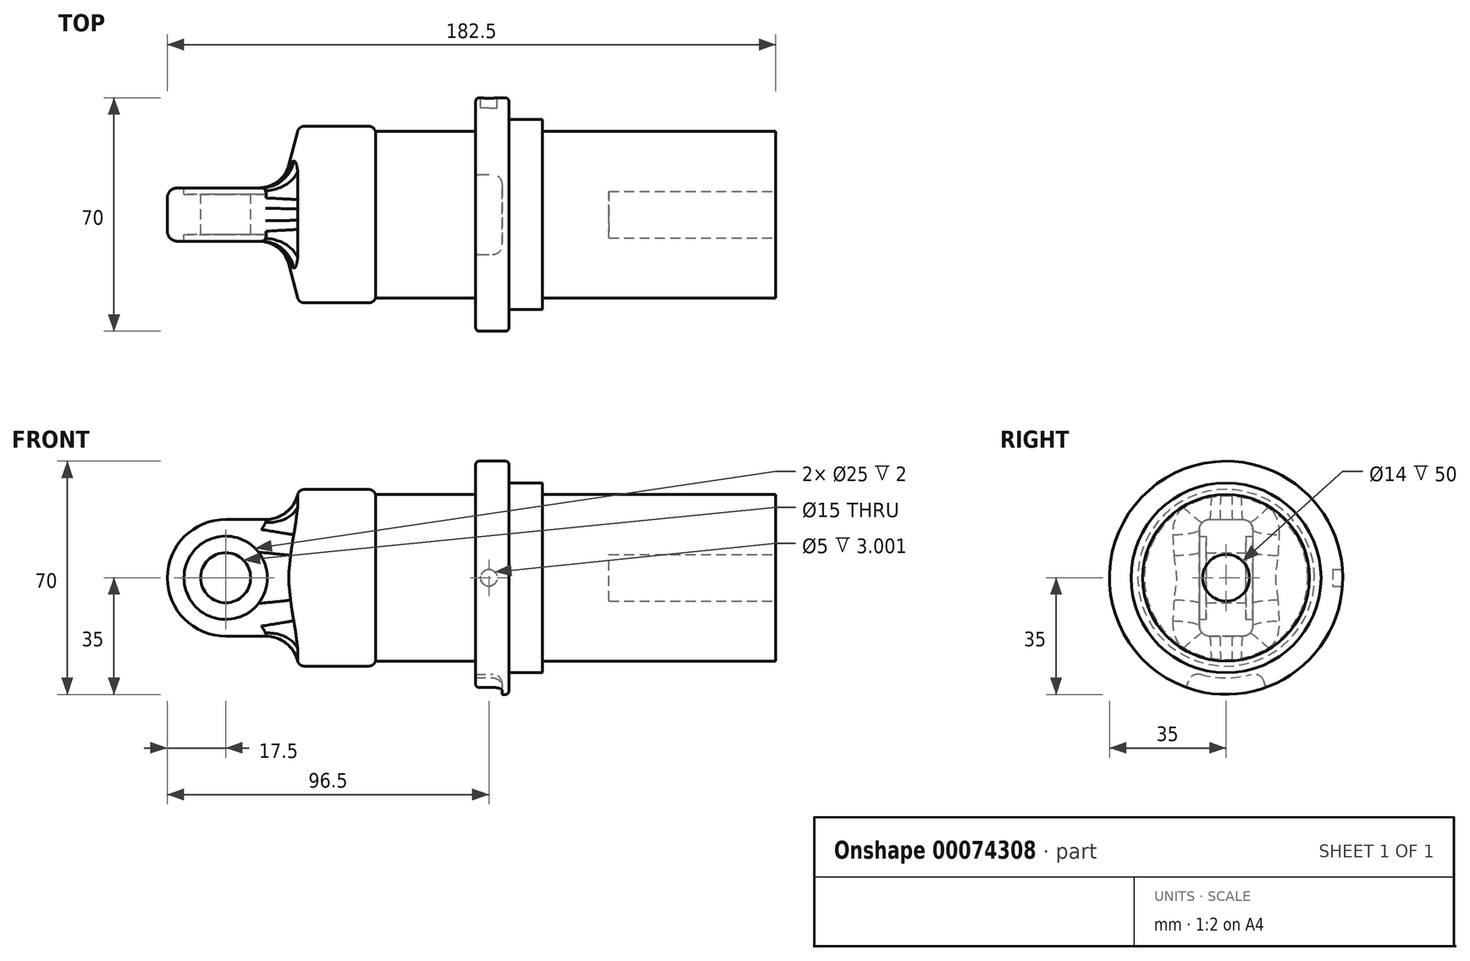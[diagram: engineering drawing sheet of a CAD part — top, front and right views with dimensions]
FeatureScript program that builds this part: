
annotation { "Feature Type Name" : "Feature", "Feature Type Description" : "" }
export const myFeature = defineFeature(function(context is Context, id is Id, definition is map)
    precondition{}
    {
        {
            var Q0;
            Q0=qCreatedBy(makeId("Front.planeOp"),FACE);
            var sketch = newSketch(context, id + "F0", { "sketchPlane" : qUnion([Q0])});
            skArc(sketch, "E0", {"start": v(0, 17.5) * mm, "mid": v(-17.5, 0) * mm, "end": v(0, -17.5) * mm});
            skCircle(sketch, "E1", {"center": v(0, 0) * mm, "radius": 12.5 * mm});
            skLineSegment(sketch, "E2", {"start": v(0, 17.5) * mm, "end": v(25, 17.5) * mm});
            skLineSegment(sketch, "E3", {"start": v(0, -17.5) * mm, "end": v(25, -17.5) * mm});
            skLineSegment(sketch, "E4", {"start": v(25, 17.5) * mm, "end": v(25, -17.5) * mm});
            skSolve(sketch);
        }
        {
            var Q0;
            Q0=makeQuery(id+"F0.imprint","IMPRINT",FACE,{"disambiguationData":[TD([[makeQuery(id+"F0.imprint","IMPRINT",EDGE,{"derivedFrom":sQuery(id+"F0.wireOp",EDGE,"E0")}),1.0]])]});
            extrude(context, id + "F1", {"entities" : qUnion([Q0]), "depth" : 16 * mm, "symmetric" : true});
        }
        {
            var Q0;
            Q0=qCreatedBy(makeId("Top.planeOp"),FACE);
            var sketch = newSketch(context, id + "F2", { "sketchPlane" : qUnion([Q0])});
            skLineSegment(sketch, "E5", {"start": v(0, 0) * mm, "end": v(85.18, 0) * mm, "construction": true});
            skLineSegment(sketch, "E6", {"start": v(45, 0) * mm, "end": v(45, 24.5) * mm});
            skLineSegment(sketch, "E7", {"start": v(43, 26.5) * mm, "end": v(23.54, 26.5) * mm});
            skLineSegment(sketch, "E8", {"start": v(21.6, 25.01) * mm, "end": v(15, 0) * mm});
            skPoint(sketch, "E9.visualSharp", {"position": v(45, 26.5) * mm});
            skArc(sketch, "E9.filletArc", {"start": v(45, 24.5) * mm, "mid": v(44.41, 25.91) * mm, "end": v(43, 26.5) * mm});
            skPoint(sketch, "E10.visualSharp", {"position": v(22, 26.5) * mm});
            skArc(sketch, "E10.filletArc", {"start": v(23.54, 26.5) * mm, "mid": v(22.32, 26.08) * mm, "end": v(21.6, 25.01) * mm});
            skLineSegment(sketch, "E11", {"start": v(45, 0) * mm, "end": v(15, 0) * mm});
            skSolve(sketch);
        }
        {
            var Q0;
            Q0=makeQuery(id+"F2.imprint","IMPRINT",FACE,{"disambiguationData":[TD([[makeQuery(id+"F2.imprint","IMPRINT",EDGE,{"derivedFrom":sQuery(id+"F2.wireOp",EDGE,"E6")}),1.0]])]});
            var Q1;
            Q1=sQuery(id+"F2.wireOp",EDGE,"E5");
            revolve(context, id + "F3", {"operationType" : NewBodyOperationType.ADD, "entities" : qUnion([Q0]), "axis" : qUnion([Q1]), "revolveType" : RevolveType.FULL});
        }
        {
            var Q0;
            Q0=makeQuery(id+"F1.opExtrude","CAP_EDGE",EDGE,{"disambiguationData":[OSD([sQuery(id+"F0.wireOp",EDGE,"E3")])],"isStart":true});
            var Q1;
            Q1=makeQuery(id+"F1.opExtrude","CAP_EDGE",EDGE,{"disambiguationData":[OSD([sQuery(id+"F0.wireOp",EDGE,"E3")])],"isStart":false});
            fillet(context, id + "F4", {"entities" : qUnion([Q0, Q1]), "radius" : 3 * mm, "tangentPropagation" : true, "allowEdgeOverflow" : false});
        }
        {
            var Q0;
            Q0=makeQuery(id+"F3.boolean.opBoolean","INTERSECT",EDGE,{"derivedFrom":[makeQuery(id+"F1.opExtrude","SWEPT_FACE",FACE,{"disambiguationData":[OSD([sQuery(id+"F0.wireOp",EDGE,"E3")])]}),makeQuery(id+"F3.opRevolve","SWEPT_FACE",FACE,{"disambiguationData":[OSD([sQuery(id+"F2.wireOp",EDGE,"E8")])]})]});
            fillet(context, id + "F5", {"entities" : qUnion([Q0]), "radius" : 10 * mm, "tangentPropagation" : true, "allowEdgeOverflow" : false});
        }
        {
            var Q0;
            Q0=qCreatedBy(makeId("Front.planeOp"),FACE);
            var sketch = newSketch(context, id + "F6", { "sketchPlane" : qUnion([Q0])});
            skCircle(sketch, "E12", {"center": v(0, 0) * mm, "radius": 7.5 * mm});
            skCircle(sketch, "E13", {"center": v(0, 0) * mm, "radius": 12.5 * mm});
            skSolve(sketch);
        }
        {
            var Q0;
            Q0 = qSketchRegion(id + "F6", true);
            extrude(context, id + "F7", {"entities" : qUnion([Q0]), "operationType" : NewBodyOperationType.ADD, "depth" : 12 * mm, "symmetric" : true});
        }
        {
            var Q0;
            Q0=makeQuery(id+"F3.opRevolve","SWEPT_FACE",FACE,{"disambiguationData":[OSD([sQuery(id+"F2.wireOp",EDGE,"E6")])]});
            var sketch = newSketch(context, id + "F8", { "sketchPlane" : qUnion([Q0])});
            skCircle(sketch, "E14", {"center": v(0, 0) * mm, "radius": 25 * mm});
            skSolve(sketch);
        }
        {
            var Q0;
            Q0 = qSketchRegion(id + "F8", true);
            extrude(context, id + "F9", {"entities" : qUnion([Q0]), "operationType" : NewBodyOperationType.ADD, "depth" : 120 * mm});
        }
        {
            var Q0;
            Q0=makeQuery(id+"F9.opExtrude","CAP_FACE",FACE,{"disambiguationData":[OSD([sQuery(id+"F8.wireOp",EDGE,"E14")])],"isStart":false});
            var sketch = newSketch(context, id + "F10", { "sketchPlane" : qUnion([Q0])});
            skCircle(sketch, "E15", {"center": v(0, 0) * mm, "radius": 7 * mm});
            skSolve(sketch);
        }
        {
            var Q0;
            Q0 = qSketchRegion(id + "F10", true);
            extrude(context, id + "F11", {"entities" : qUnion([Q0]), "operationType" : NewBodyOperationType.REMOVE, "oppositeDirection" : true, "depth" : 50 * mm});
        }
        {
            var Q0;
            Q0=makeQuery(id+"F9.opExtrude","CAP_FACE",FACE,{"disambiguationData":[OSD([sQuery(id+"F8.wireOp",EDGE,"E14")])],"isStart":false});
            cPlane(context, id + "F12", {"entities" : qUnion([Q0]), "cplaneType" : CPlaneType.OFFSET, "offset" : 80 * mm, "oppositeDirection" : true, "width" : 150 * mm, "height" : 150 * mm});
        }
        {
            var Q0;
            Q0=qCreatedBy(id+"F12.planeOp",FACE);
            var sketch = newSketch(context, id + "F13", { "sketchPlane" : qUnion([Q0])});
            skCircle(sketch, "E16.0", {"center": v(0, 0) * mm, "radius": 25 * mm});
            skCircle(sketch, "E17", {"center": v(0, 0) * mm, "radius": 28.5 * mm});
            skSolve(sketch);
        }
        {
            var Q0;
            Q0 = qSketchRegion(id + "F13", true);
            extrude(context, id + "F14", {"entities" : qUnion([Q0]), "operationType" : NewBodyOperationType.ADD, "depth" : 10 * mm});
        }
        {
            var Q0;
            Q0=makeQuery(id+"F14.opExtrude","CAP_FACE",FACE,{"disambiguationData":[OSD([sQuery(id+"F13.wireOp",EDGE,"E16.0"),sQuery(id+"F13.wireOp",EDGE,"E17")])],"isStart":true});
            var sketch = newSketch(context, id + "F15", { "sketchPlane" : qUnion([Q0])});
            skCircle(sketch, "E18.0", {"center": v(0, 0) * mm, "radius": 25 * mm});
            skCircle(sketch, "E19", {"center": v(0, 0) * mm, "radius": 35 * mm});
            skSolve(sketch);
        }
        {
            var Q0;
            Q0 = qSketchRegion(id + "F15", true);
            extrude(context, id + "F16", {"entities" : qUnion([Q0]), "operationType" : NewBodyOperationType.ADD, "depth" : 10 * mm});
        }
        {
            var Q0;
            Q0=qCreatedBy(makeId("Front.planeOp"),FACE);
            var sketch = newSketch(context, id + "F17", { "sketchPlane" : qUnion([Q0])});
            skLineSegment(sketch, "E20", {"start": v(0, 0) * mm, "end": v(172.26, 0) * mm, "construction": true});
            skLineSegment(sketch, "E21.0", {"start": v(75, -35) * mm, "end": v(75, 35) * mm, "construction": true});
            skLineSegment(sketch, "E22.bottom", {"start": v(75, -35) * mm, "end": v(83, -35) * mm});
            skLineSegment(sketch, "E22.top", {"start": v(75, -30) * mm, "end": v(83, -30) * mm});
            skLineSegment(sketch, "E22.left", {"start": v(75, -35) * mm, "end": v(75, -30) * mm});
            skLineSegment(sketch, "E22.right", {"start": v(83, -35) * mm, "end": v(83, -30) * mm});
            skSolve(sketch);
        }
        {
            var Q0;
            Q0 = qSketchRegion(id + "F17", true);
            var Q1;
            Q1=sQuery(id+"F17.wireOp",EDGE,"E20");
            revolve(context, id + "F18", {"operationType" : NewBodyOperationType.REMOVE, "entities" : qUnion([Q0]), "axis" : qUnion([Q1]), "revolveType" : RevolveType.SYMMETRIC, "oppositeDirection" : true, "angle" : 40 * degree});
        }
        {
            var Q0;
            Q0=makeQuery(id+"F18.boolean.opBoolean","COPY",EDGE,{"derivedFrom":makeQuery(id+"F18.opRevolve","SWEPT_EDGE",EDGE,{"disambiguationData":[OSD([sQuery(id+"F17.wireOp",EDGE,"E22.top"),sQuery(id+"F17.wireOp",EDGE,"E22.right")])]})});
            var Q1;
            Q1=makeQuery(id+"F18.boolean.opBoolean","COPY",EDGE,{"derivedFrom":makeQuery(id+"F18.opRevolve","CAP_EDGE",EDGE,{"disambiguationData":[OSD([sQuery(id+"F17.wireOp",EDGE,"E22.right")])],"isStart":false})});
            var Q2;
            Q2=makeQuery(id+"F18.boolean.opBoolean","COPY",EDGE,{"derivedFrom":makeQuery(id+"F18.opRevolve","CAP_EDGE",EDGE,{"disambiguationData":[OSD([sQuery(id+"F17.wireOp",EDGE,"E22.top")])],"isStart":false})});
            var Q3;
            Q3=makeQuery(id+"F18.boolean.opBoolean","COPY",EDGE,{"derivedFrom":makeQuery(id+"F18.opRevolve","CAP_EDGE",EDGE,{"disambiguationData":[OSD([sQuery(id+"F17.wireOp",EDGE,"E22.top")])],"isStart":true})});
            var Q4;
            Q4=makeQuery(id+"F18.boolean.opBoolean","COPY",EDGE,{"derivedFrom":makeQuery(id+"F18.opRevolve","CAP_EDGE",EDGE,{"disambiguationData":[OSD([sQuery(id+"F17.wireOp",EDGE,"E22.right")])],"isStart":true})});
            fillet(context, id + "F19", {"entities" : qUnion([Q0, Q1, Q2, Q3, Q4]), "radius" : 3 * mm, "tangentPropagation" : true, "allowEdgeOverflow" : false});
        }
        {
            var Q0;
            Q0=qCreatedBy(makeId("Front.planeOp"),FACE);
            cPlane(context, id + "F20", {"entities" : qUnion([Q0]), "cplaneType" : CPlaneType.OFFSET, "offset" : 40 * mm, "oppositeDirection" : true, "width" : 150 * mm, "height" : 150 * mm});
        }
        {
            var Q0;
            Q0=qCreatedBy(id+"F20.planeOp",FACE);
            var sketch = newSketch(context, id + "F21", { "sketchPlane" : qUnion([Q0])});
            skCircle(sketch, "E23", {"center": v(79, 0) * mm, "radius": 2.5 * mm});
            skSolve(sketch);
        }
        {
            var Q0;
            Q0 = qSketchRegion(id + "F21", true);
            extrude(context, id + "F22", {"entities" : qUnion([Q0]), "operationType" : NewBodyOperationType.REMOVE, "depth" : 8 * mm});
        }
        {
            var Q0;
            Q0=makeQuery(id+"F16.opExtrude","CAP_EDGE",EDGE,{"disambiguationData":[OSD([sQuery(id+"F15.wireOp",EDGE,"E19")])],"isStart":true});
            fillet(context, id + "F23", {"entities" : qUnion([Q0]), "radius" : 1 * mm, "tangentPropagation" : true, "allowEdgeOverflow" : false});
        }
        {
            var Q0;
            {var subQ0=sQuery(id+"F15.wireOp",EDGE,"E19");var subQ3=sQuery(id+"F17.wireOp",EDGE,"E22.right");var subQ4=sQuery(id+"F17.wireOp",EDGE,"E22.left");var subQ5=sQuery(id+"F17.wireOp",EDGE,"E22.top");var subQ6=sQuery(id+"F17.wireOp",EDGE,"E22.bottom");var subQ7=makeQuery(id+"FgvS7bpNY4bW3Lr_1.4.F18.opRevolve","CAP_FACE",FACE,{"disambiguationData":[OSD([subQ6,subQ5,subQ4,subQ3])],"isStart":false});var subQ8=makeQuery(id+"F18.boolean.opBoolean","COPY",FACE,{"derivedFrom":makeQuery(id+"F18.opRevolve","CAP_FACE",FACE,{"disambiguationData":[OSD([subQ6,subQ5,subQ4,subQ3])],"isStart":true})});Q0=makeQuery(id+"FgvS7bpNY4bW3Lr_1.5.F18.boolean.opBoolean","SPLIT",EDGE,{"disambiguationData":[TD([makeQuery(id+"FgvS7bpNY4bW3Lr_1.4.F18.boolean.opBoolean","COPY",FACE,{"derivedFrom":subQ7})])],"derivedFrom":makeQuery(id+"FgvS7bpNY4bW3Lr_1.4.F18.boolean.opBoolean","SPLIT",EDGE,{"disambiguationData":[TD([subQ8])],"derivedFrom":makeQuery(id+"FgvS7bpNY4bW3Lr_1.3.F18.boolean.opBoolean","SPLIT",EDGE,{"disambiguationData":[TD([subQ8])],"derivedFrom":makeQuery(id+"FgvS7bpNY4bW3Lr_1.2.F18.boolean.opBoolean","SPLIT",EDGE,{"disambiguationData":[TD([subQ8])],"derivedFrom":makeQuery(id+"FgvS7bpNY4bW3Lr_1.1.F18.boolean.opBoolean","SPLIT",EDGE,{"disambiguationData":[TD([subQ8])],"derivedFrom":makeQuery(id+"F16.opExtrude","CAP_EDGE",EDGE,{"disambiguationData":[OSD([subQ0])],"isStart":false})})})})})});}
            var Q1;
            {var subQ0=sQuery(id+"F15.wireOp",EDGE,"E19");var subQ3=sQuery(id+"F17.wireOp",EDGE,"E22.right");var subQ4=sQuery(id+"F17.wireOp",EDGE,"E22.left");var subQ5=sQuery(id+"F17.wireOp",EDGE,"E22.top");var subQ6=sQuery(id+"F17.wireOp",EDGE,"E22.bottom");var subQ7=makeQuery(id+"F18.boolean.opBoolean","COPY",FACE,{"derivedFrom":makeQuery(id+"F18.opRevolve","CAP_FACE",FACE,{"disambiguationData":[OSD([subQ6,subQ5,subQ4,subQ3])],"isStart":true})});Q1=makeQuery(id+"FgvS7bpNY4bW3Lr_1.5.F18.boolean.opBoolean","SPLIT",EDGE,{"disambiguationData":[TD([subQ7])],"derivedFrom":makeQuery(id+"FgvS7bpNY4bW3Lr_1.4.F18.boolean.opBoolean","SPLIT",EDGE,{"disambiguationData":[TD([subQ7])],"derivedFrom":makeQuery(id+"FgvS7bpNY4bW3Lr_1.3.F18.boolean.opBoolean","SPLIT",EDGE,{"disambiguationData":[TD([subQ7])],"derivedFrom":makeQuery(id+"FgvS7bpNY4bW3Lr_1.2.F18.boolean.opBoolean","SPLIT",EDGE,{"disambiguationData":[TD([subQ7])],"derivedFrom":makeQuery(id+"FgvS7bpNY4bW3Lr_1.1.F18.boolean.opBoolean","SPLIT",EDGE,{"disambiguationData":[TD([subQ7])],"derivedFrom":makeQuery(id+"F16.opExtrude","CAP_EDGE",EDGE,{"disambiguationData":[OSD([subQ0])],"isStart":false})})})})})});}
            var Q2;
            {var subQ0=sQuery(id+"F15.wireOp",EDGE,"E19");var subQ3=sQuery(id+"F17.wireOp",EDGE,"E22.right");var subQ4=sQuery(id+"F17.wireOp",EDGE,"E22.left");var subQ5=sQuery(id+"F17.wireOp",EDGE,"E22.top");var subQ6=sQuery(id+"F17.wireOp",EDGE,"E22.bottom");var subQ7=makeQuery(id+"FgvS7bpNY4bW3Lr_1.3.F18.opRevolve","CAP_FACE",FACE,{"disambiguationData":[OSD([subQ6,subQ5,subQ4,subQ3])],"isStart":false});var subQ8=makeQuery(id+"F18.boolean.opBoolean","COPY",FACE,{"derivedFrom":makeQuery(id+"F18.opRevolve","CAP_FACE",FACE,{"disambiguationData":[OSD([subQ6,subQ5,subQ4,subQ3])],"isStart":true})});Q2=makeQuery(id+"FgvS7bpNY4bW3Lr_1.4.F18.boolean.opBoolean","SPLIT",EDGE,{"disambiguationData":[TD([makeQuery(id+"FgvS7bpNY4bW3Lr_1.3.F18.boolean.opBoolean","COPY",FACE,{"derivedFrom":subQ7})])],"derivedFrom":makeQuery(id+"FgvS7bpNY4bW3Lr_1.3.F18.boolean.opBoolean","SPLIT",EDGE,{"disambiguationData":[TD([subQ8])],"derivedFrom":makeQuery(id+"FgvS7bpNY4bW3Lr_1.2.F18.boolean.opBoolean","SPLIT",EDGE,{"disambiguationData":[TD([subQ8])],"derivedFrom":makeQuery(id+"FgvS7bpNY4bW3Lr_1.1.F18.boolean.opBoolean","SPLIT",EDGE,{"disambiguationData":[TD([subQ8])],"derivedFrom":makeQuery(id+"F16.opExtrude","CAP_EDGE",EDGE,{"disambiguationData":[OSD([subQ0])],"isStart":false})})})})});}
            var Q3;
            {var subQ0=sQuery(id+"F15.wireOp",EDGE,"E19");var subQ2=sQuery(id+"F17.wireOp",EDGE,"E22.right");var subQ3=sQuery(id+"F17.wireOp",EDGE,"E22.left");var subQ4=sQuery(id+"F17.wireOp",EDGE,"E22.top");var subQ5=sQuery(id+"F17.wireOp",EDGE,"E22.bottom");var subQ6=makeQuery(id+"FgvS7bpNY4bW3Lr_1.2.F18.opRevolve","CAP_FACE",FACE,{"disambiguationData":[OSD([subQ5,subQ4,subQ3,subQ2])],"isStart":false});var subQ8=makeQuery(id+"F18.boolean.opBoolean","COPY",FACE,{"derivedFrom":makeQuery(id+"F18.opRevolve","CAP_FACE",FACE,{"disambiguationData":[OSD([subQ5,subQ4,subQ3,subQ2])],"isStart":true})});Q3=makeQuery(id+"FgvS7bpNY4bW3Lr_1.3.F18.boolean.opBoolean","SPLIT",EDGE,{"disambiguationData":[TD([makeQuery(id+"FgvS7bpNY4bW3Lr_1.2.F18.boolean.opBoolean","COPY",FACE,{"derivedFrom":subQ6})])],"derivedFrom":makeQuery(id+"FgvS7bpNY4bW3Lr_1.2.F18.boolean.opBoolean","SPLIT",EDGE,{"disambiguationData":[TD([subQ8])],"derivedFrom":makeQuery(id+"FgvS7bpNY4bW3Lr_1.1.F18.boolean.opBoolean","SPLIT",EDGE,{"disambiguationData":[TD([subQ8])],"derivedFrom":makeQuery(id+"F16.opExtrude","CAP_EDGE",EDGE,{"disambiguationData":[OSD([subQ0])],"isStart":false})})})});}
            var Q4;
            {var subQ0=sQuery(id+"F15.wireOp",EDGE,"E19");var subQ1=sQuery(id+"F17.wireOp",EDGE,"E22.right");var subQ2=sQuery(id+"F17.wireOp",EDGE,"E22.left");var subQ3=sQuery(id+"F17.wireOp",EDGE,"E22.top");var subQ4=sQuery(id+"F17.wireOp",EDGE,"E22.bottom");Q4=makeQuery(id+"FgvS7bpNY4bW3Lr_1.1.F18.boolean.opBoolean","SPLIT",EDGE,{"disambiguationData":[TD([makeQuery(id+"F18.boolean.opBoolean","COPY",FACE,{"derivedFrom":makeQuery(id+"F18.opRevolve","CAP_FACE",FACE,{"disambiguationData":[OSD([subQ4,subQ3,subQ2,subQ1])],"isStart":false})})])],"derivedFrom":makeQuery(id+"F16.opExtrude","CAP_EDGE",EDGE,{"disambiguationData":[OSD([subQ0])],"isStart":false})});}
            var Q5;
            {var subQ0=sQuery(id+"F15.wireOp",EDGE,"E19");var subQ2=sQuery(id+"F17.wireOp",EDGE,"E22.right");var subQ3=sQuery(id+"F17.wireOp",EDGE,"E22.left");var subQ4=sQuery(id+"F17.wireOp",EDGE,"E22.top");var subQ5=sQuery(id+"F17.wireOp",EDGE,"E22.bottom");var subQ7=makeQuery(id+"FgvS7bpNY4bW3Lr_1.1.F18.opRevolve","CAP_FACE",FACE,{"disambiguationData":[OSD([subQ5,subQ4,subQ3,subQ2])],"isStart":false});Q5=makeQuery(id+"FgvS7bpNY4bW3Lr_1.2.F18.boolean.opBoolean","SPLIT",EDGE,{"disambiguationData":[TD([makeQuery(id+"FgvS7bpNY4bW3Lr_1.1.F18.boolean.opBoolean","COPY",FACE,{"derivedFrom":subQ7})])],"derivedFrom":makeQuery(id+"FgvS7bpNY4bW3Lr_1.1.F18.boolean.opBoolean","SPLIT",EDGE,{"disambiguationData":[TD([makeQuery(id+"F18.boolean.opBoolean","COPY",FACE,{"derivedFrom":makeQuery(id+"F18.opRevolve","CAP_FACE",FACE,{"disambiguationData":[OSD([subQ5,subQ4,subQ3,subQ2])],"isStart":true})})])],"derivedFrom":makeQuery(id+"F16.opExtrude","CAP_EDGE",EDGE,{"disambiguationData":[OSD([subQ0])],"isStart":false})})});}
            fillet(context, id + "F24", {"entities" : qUnion([Q0, Q1, Q2, Q3, Q4, Q5]), "radius" : 1 * mm, "tangentPropagation" : true, "allowEdgeOverflow" : false});
        }
    });
